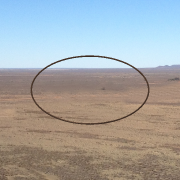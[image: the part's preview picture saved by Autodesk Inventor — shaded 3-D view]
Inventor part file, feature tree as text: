
AUTODESK INVENTOR PART (.ipt)
format: ipt  version: 2013 SP2 (Build 170200200, 200)  size: 154,112 bytes
history: native  units: in
note: dims shown in document units (in); Inventor stores cm internally (conversion verified against a paired STEP export)
features: revolve x1, sketch x1
ambient origin geometry x8: Origin, YZ Plane, XZ Plane, XY Plane, X Axis, Y Axis, Z Axis, Center Point
bodies: Solid1 (feature_tree)
feature tree (2):
  revolve  "Revolution1"  [1 undecoded]
  sketch  "Sketch1"  dims[d0=0.3in d1=12.0in d2=90.0deg]
note: 1 required parameter value undecoded (feature->parameter linkage not recoverable at this tier; creation-order binding heuristic only, values carry confidence <= 0.55)
